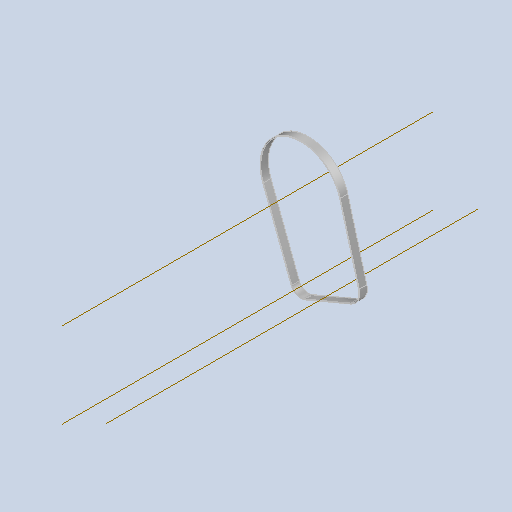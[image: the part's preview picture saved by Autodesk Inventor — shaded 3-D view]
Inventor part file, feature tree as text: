
AUTODESK INVENTOR PART (.ipt)
format: ipt  version: 2024 (Build 280153000, 153)  size: 107,008 bytes
history: native  units: mm (DEFAULTED — no unit token found)
features: other x5, plane x2, sketch x1, sweep x1
ambient origin geometry x8: Origin, YZ Plane, XZ Plane, XY Plane, X Axis, Y Axis, Z Axis, Center Point
bodies: Solid1 (feature_tree)
feature tree (9):
  sketch  "Sketch Path"  dims[d0=6.0mm d2=0.0mm d4=0.3mm d5=0.3mm d6=0.0mm d7=0.0mm d8=0.0mm d9=0.0mm d10=0.0mm d11=0.0mm d12=0.0mm]
  other  "Cross Section Plane"
  other  "Work Axis1"
  other  "Work Axis2"
  other  "Work Axis3"
  plane  "Work Plane2"
  plane  "Work Plane3"
  sweep  "Belt"
  other  "Cross Section"
